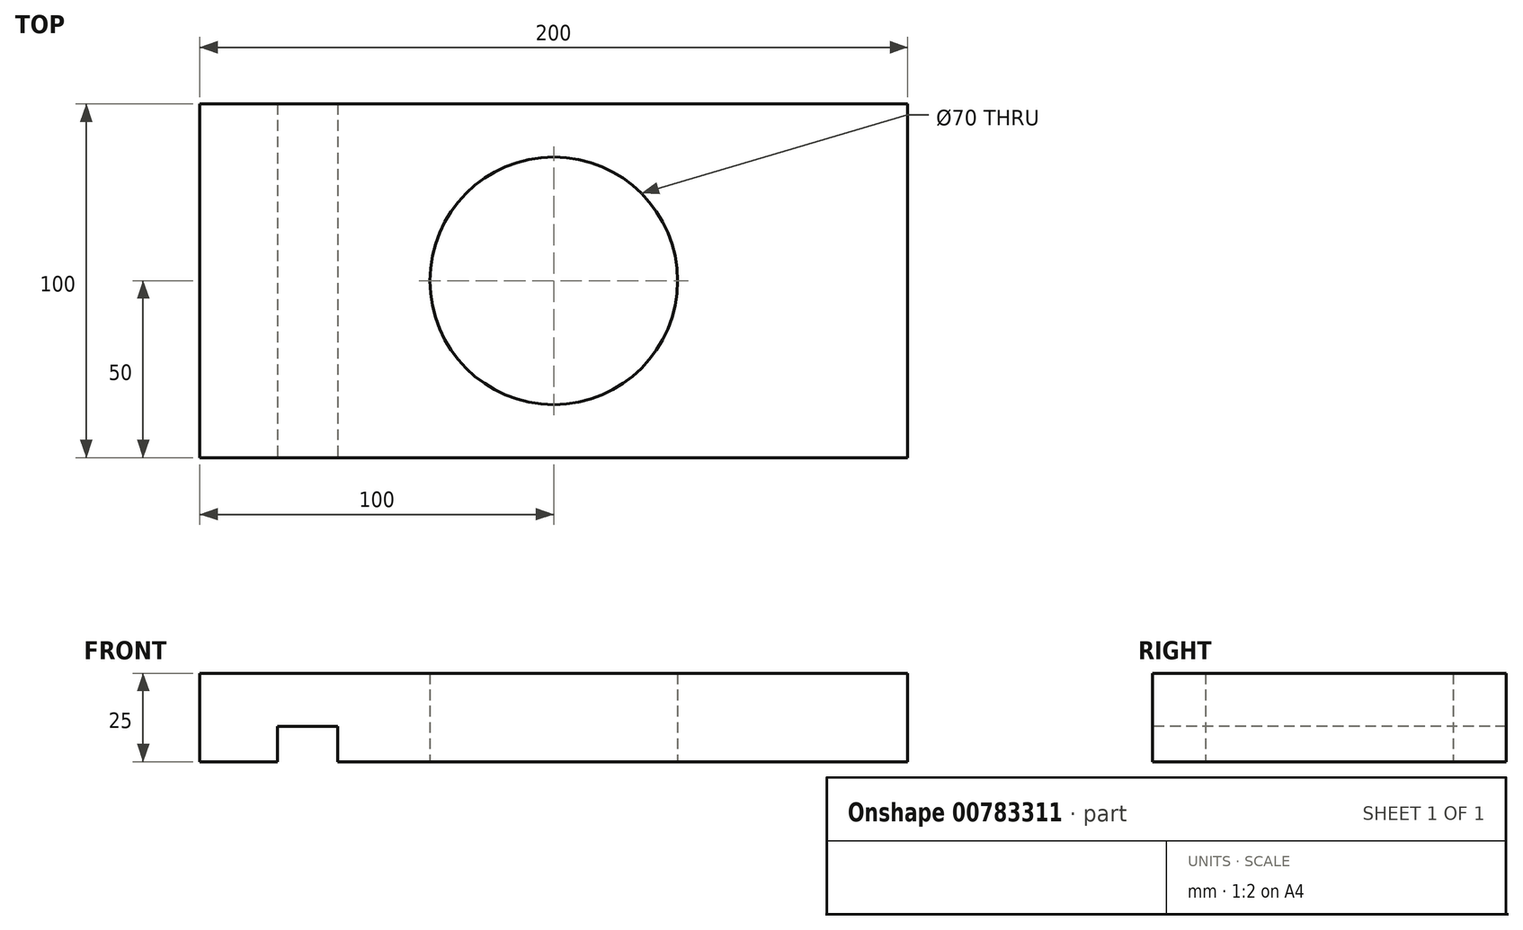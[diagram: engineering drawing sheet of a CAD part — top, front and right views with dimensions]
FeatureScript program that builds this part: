
annotation { "Feature Type Name" : "Feature", "Feature Type Description" : "" }
export const myFeature = defineFeature(function(context is Context, id is Id, definition is map)
    precondition{}
    {
        {
            var Q0;
            Q0=qCreatedBy(makeId("Top.planeOp"),FACE);
            var sketch = newSketch(context, id + "F0", { "sketchPlane" : qUnion([Q0])});
            skLineSegment(sketch, "E0.bottom", {"start": v(-100, 50) * mm, "end": v(100, 50) * mm});
            skLineSegment(sketch, "E0.top", {"start": v(-100, -50) * mm, "end": v(100, -50) * mm});
            skLineSegment(sketch, "E0.left", {"start": v(-100, 50) * mm, "end": v(-100, -50) * mm});
            skLineSegment(sketch, "E0.right", {"start": v(100, 50) * mm, "end": v(100, -50) * mm});
            skPoint(sketch, "E0.middle", {"position": v(0, 0) * mm});
            skCircle(sketch, "E1", {"center": v(0, 0) * mm, "radius": 35 * mm});
            skSolve(sketch);
        }
        {
            var Q0;
            Q0 = qSketchRegion(id + "F0", true);
            extrude(context, id + "F1", {"entities" : qUnion([Q0]), "depth" : 25 * mm, "offsetDistance" : 25 * mm});
        }
        {
            var Q0;
            Q0=qCreatedBy(makeId("Top.planeOp"),FACE);
            var sketch = newSketch(context, id + "F2", { "sketchPlane" : qUnion([Q0])});
            skLineSegment(sketch, "E2.0", {"start": v(-100, 50) * mm, "end": v(100, 50) * mm});
            skLineSegment(sketch, "E3.0.0", {"start": v(-100, 50) * mm, "end": v(-100, -50) * mm});
            skLineSegment(sketch, "E3.0.1", {"start": v(-100, -50) * mm, "end": v(100, -50) * mm});
            skLineSegment(sketch, "E3.0.2", {"start": v(100, -50) * mm, "end": v(100, 50) * mm});
            skLineSegment(sketch, "E3.0.3", {"start": v(100, 50) * mm, "end": v(-100, 50) * mm});
            skLineSegment(sketch, "E4.bottom", {"start": v(-78.1, 50) * mm, "end": v(-61.1, 50) * mm});
            skLineSegment(sketch, "E4.top", {"start": v(-78.1, -50) * mm, "end": v(-61.1, -50) * mm});
            skLineSegment(sketch, "E4.left", {"start": v(-78.1, 50) * mm, "end": v(-78.1, -50) * mm});
            skLineSegment(sketch, "E4.right", {"start": v(-61.1, 50) * mm, "end": v(-61.1, -50) * mm});
            skSolve(sketch);
        }
        {
            var Q0;
            {var subQ2=sQuery(id+"F2.wireOp",EDGE,"E4.left");Q0=makeQuery(id+"F2.imprint","IMPRINT",FACE,{"disambiguationData":[TD([[makeQuery(id+"F2.imprint","IMPRINT",EDGE,{"derivedFrom":subQ2}),1.0]])]});}
            extrude(context, id + "F3", {"entities" : qUnion([Q0]), "operationType" : NewBodyOperationType.REMOVE, "depth" : 10 * mm, "offsetDistance" : 25 * mm});
        }
    });
